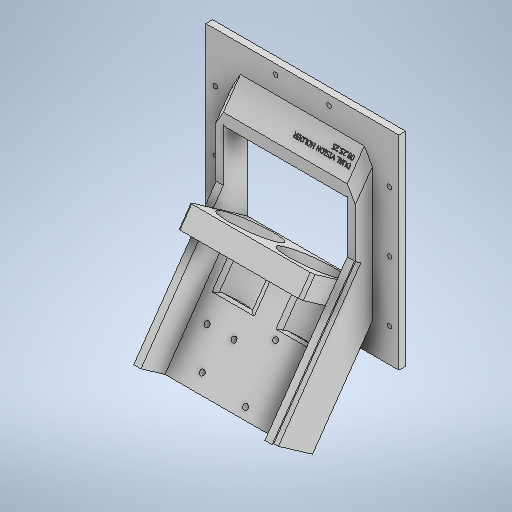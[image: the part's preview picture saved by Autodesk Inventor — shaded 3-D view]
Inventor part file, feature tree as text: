
AUTODESK INVENTOR PART (.ipt)
format: ipt  version: 2025.3 (Build 293356030, 356C)  size: 1,626,112 bytes
history: native  units: in
note: dims shown in document units (in); Inventor stores cm internally (conversion verified against a paired STEP export)
features: sketch x58, extrude x53, projected_geometry x13, plane x5, chamfer x3, move_body x1, hole x1
ambient origin geometry x8: Origin, YZ Plane, XZ Plane, XY Plane, X Axis, Y Axis, Z Axis, Center Point
bodies: Solid1 (feature_tree)
feature tree (134):
  extrude  "Extrusion1"  Depth=0.1969in TaperAngle=0.0deg
  move_body  "Move Body1"
  plane  "Work Plane1"
  sketch  "Sketch5"  dims[d5=1.7717in d6=1.7717in d7=1.7717in d8=1.7717in d9=0.8108in d10=90.0deg d11=0.0787in d12=0.3701in d13=0.4252in d14=0.1362in d15=-0.0984in d16=-0.0591in d17=0.0in]
  plane  "Work Plane2"
  extrude  "Extrusion4"  TaperAngle=0.0deg  [1 undecoded]
  extrude  "Extrusion6"  Depth=0.2405in
  extrude  "Extrusion8"  Depth=2.7559in TaperAngle=0.0deg
  chamfer  "Chamfer1"  [1 undecoded]
  extrude  "Extrusion11"  Depth=0.2362in
  plane  "Work Plane3"
  extrude  "Extrusion13"  Depth=0.1969in TaperAngle=0.0deg
  plane  "Work Plane4"
  plane  "Work Plane6"
  extrude  "Extrusion21"  Depth=0.5027in
  extrude  "Extrusion22"  Depth=0.5027in
  extrude  "Extrusion25"  Depth=1.1811in TaperAngle=0.0deg
  extrude  "Extrusion26"  Depth=0.1969in
  sketch  "Sketch33"  dims[d100=3.6403in d101=2.7717in]
  extrude  "Extrusion27"  Depth=0.2362in TaperAngle=0.0deg
  extrude  "Extrusion29"  Depth=3.6403in
  extrude  "Extrusion28"  Depth=0.6299in TaperAngle=0.0deg
  sketch  "Sketch36"  dims[d124=0.9712in d125=0.0in d126=0.5906in d127=0.0in]
  extrude  "Extrusion30"  Depth=0.7874in
  extrude  "Extrusion31"  Depth=0.5906in TaperAngle=0.0deg
  sketch  "Sketch39"  dims[d164=0.1181in d165=0.0in d168=0.5906in d169=0.0in]
  extrude  "Extrusion35"  Depth=11.3469in TaperAngle=0.0deg
  sketch  "Sketch45"  dims[d176=0.7313in d177=0.0in d186=0.0in d187=0.0in]
  extrude  "Extrusion37"  Depth=0.1181in TaperAngle=0.0deg
  extrude  "Extrusion38"  Depth=0.1181in TaperAngle=0.0deg
  extrude  "Extrusion40"  TaperAngle=0.0deg  [1 undecoded]
  extrude  "Extrusion41"  TaperAngle=0.0deg  [1 undecoded]
  extrude  "Extrusion43"  TaperAngle=0.0deg  [1 undecoded]
  extrude  "Extrusion44"  Depth=0.0394in TaperAngle=0.0deg
  extrude  "Extrusion46"  Depth=3.9671in TaperAngle=0.0deg
  extrude  "Name Extrusion"  Depth=0.1969in
  extrude  "Extrusion48"  TaperAngle=60.0deg  [1 undecoded]
  sketch  "Sketch61"  dims[d257=0.1181in d258=0.0in d259=0.0787in d260=0.0in]
  extrude  "Extrusion50"  Depth=0.1969in
  extrude  "Extrusion51"  Depth=0.3937in
  extrude  "Extrusion52"  Depth=0.3937in
  extrude  "Extrusion53"  Depth=0.0787in TaperAngle=0.0deg
  extrude  "Extrusion54"  Depth=0.3937in TaperAngle=0.0deg
  extrude  "Extrusion57"  TaperAngle=0.0deg  [1 undecoded]
  extrude  "Extrusion59"  Depth=0.9449in
  extrude  "Extrusion60"  TaperAngle=0.0deg  [1 undecoded]
  extrude  "Event Cam Hole"  Depth=1.1614in
  extrude  "Extrusion62"  Depth=0.6299in TaperAngle=0.0deg
  extrude  "Extrusion63"  Depth=0.1969in TaperAngle=0.0deg
  extrude  "Extrusion64"  Depth=0.1181in TaperAngle=0.0deg
  extrude  "Extrusion65"  Depth=0.1575in
  extrude  "Extrusion70"  Depth=0.1575in
  extrude  "Extrusion74"  Depth=0.1575in
  extrude  "Extrusion76"  Depth=0.1575in
  extrude  "Extrusion77"  Depth=3.6405in
  extrude  "Extrusion78"  Depth=0.2756in
  extrude  "Extrusion81"  Depth=0.1181in TaperAngle=0.0deg
  chamfer  "Chamfer3"  Distance=0.1956in
  extrude  "Extrusion82"  TaperAngle=0.0deg  [1 undecoded]
  extrude  "Extrusion83"  Depth=0.0787in TaperAngle=45.0deg
  extrude  "Extrusion84"  Depth=0.3543in
  extrude  "Extrusion85"  Depth=0.3543in
  extrude  "Extrusion86"  Depth=0.1181in
  chamfer  "Chamfer4"  Distance=0.0984in
  extrude  "Extrusion87"  TaperAngle=0.0deg  [1 undecoded]
  extrude  "Extrusion88"  Depth=1.0236in TaperAngle=0.0deg
  sketch  "Sketch107"  dims[d398=0.3937in]
  extrude  "Extrusion89"  Depth=0.3937in TaperAngle=0.0deg
  extrude  "Extrusion90"  Depth=0.3937in
  sketch  "Sketch1"  dims[d1=0.5512in d2=0.1969in d3=0.0in]
  sketch  "Sketch6"  dims[d18=0.2749in d24=0.2405in]
  sketch  "Sketch8"  dims[d25=2.7559in d26=0.0in d29=2.5591in d30=0.0in d36=0.0in d37=0.0in]
  sketch  "Sketch12"  dims[d42=0.2362in d43=0.2362in]
  sketch  "Sketch15"  dims[d52=0.2362in d53=0.0787in d54=45.0deg d55=0.1969in d56=0.0in]
  sketch  "Sketch17"  dims[d59=0.5906in d60=0.0in d76=0.5027in]
  sketch  "Sketch27"  dims[d77=0.5027in d78=0.5027in]
  sketch  "Sketch28"  dims[d79=0.5027in d81=1.1811in d82=0.0in]
  sketch  "Sketch31"  dims[d83=0.0in d84=0.0in d91=0.1969in]
  sketch  "Sketch32"  dims[d94=0.2362in d95=0.0in d96=0.2362in d97=0.0in]
  sketch  "Sketch34"  dims[d112=1.9685in d113=0.6299in d114=0.0in]
  sketch  "Sketch35"  dims[d115=0.1575in d117=0.1575in d122=0.7874in d123=0.9331in]
  sketch  "Sketch37"  dims[d128=11.3469in d129=0.0in d130=11.3469in d131=0.0in]
  sketch  "Sketch38"  dims[d141=0.6299in d156=0.1181in d157=0.0in]
  sketch  "Sketch44"  dims[d170=4.7244in d171=0.0in d174=0.0in d175=0.0in]
  projected_geometry  "Projected Loop2"
  projected_geometry  "Projected Loop3"
  projected_geometry  "Projected Loop5"
  sketch  "Sketch47"  dims[d188=0.0in d189=0.0in d194=0.0in d195=0.0in]
  sketch  "Sketch49"  dims[d198=0.0591in d199=0.0in d200=0.0394in d201=0.0in]
  sketch  "Sketch50"  dims[d235=6.1063in d236=0.0in d244=3.9671in d245=0.0in]
  sketch  "Sketch52"  dims[d246=0.9963in d248=0.1969in]
  sketch  "Sketch53"  dims[d249=0.1378in d250=60.0deg]
  sketch  "Sketch56"  dims[d251=0.1969in d252=0.1378in]
  sketch  "Sketch58"  dims[d253=60.0deg d254=0.3937in]
  sketch  "Sketch59"  dims[d255=0.3937in d256=0.3937in]
  sketch  "Sketch63"  dims[d261=1.9685in d262=0.0in d271=0.3937in d272=0.0in]
  sketch  "Sketch64"  dims[d275=0.3937in d276=0.0in d277=0.0in d278=0.0in]
  sketch  "Sketch65"  dims[d279=1.6142in d280=0.9449in]
  sketch  "Sketch66"  dims[d281=1.2598in d282=0.0in d283=0.0in]
  sketch  "Sketch67"  dims[d284=1.5748in d287=1.1614in]
  sketch  "Sketch70"  dims[d288=0.8512in d289=0.6299in d290=0.0in]
  sketch  "Sketch72"  dims[d291=2.9921in d292=0.0in d293=0.1969in d294=0.0in]
  sketch  "Sketch75"  dims[d295=0.1181in d296=0.0in d314=0.0197in d315=0.0in]
  sketch  "Sketch76"  dims[d331=0.3937in d332=0.1575in]
  sketch  "Sketch77"  dims[d333=0.1575in d334=1.0236in]
  sketch  "Sketch79"  dims[d335=0.1575in d336=1.5354in]
  projected_geometry  "Projected Loop11"
  sketch  "Sketch80"  dims[d337=0.1575in d338=1.0236in]
  projected_geometry  "Projected Loop12"
  sketch  "Sketch81"  dims[d339=3.6405in d340=0.0in d347=0.2756in]
  sketch  "Sketch86"  dims[d348=0.2756in d349=0.2756in]
  projected_geometry  "Projected Loop14"
  sketch  "Sketch90"  dims[d351=0.2756in d352=0.1181in d353=0.0in d354=0.1956in d355=0.0in]
  sketch  "Sketch94"  dims[d356=0.0197in d357=0.0in d358=0.0in]
  sketch  "Sketch95"  dims[d363=3.6403in d364=0.0in d365=0.0787in d366=0.0787in d367=45.0deg]
  projected_geometry  "Projected Loop15"
  projected_geometry  "Projected Loop16"
  sketch  "Sketch96"  dims[d371=0.3543in d372=0.3543in]
  sketch  "Sketch99"  dims[d373=0.3543in d374=0.3543in]
  sketch  "Sketch100"  dims[d375=0.1181in d376=0.1181in d377=0.0984in d378=0.0in]
  sketch  "Sketch101"  dims[d379=0.067in d380=0.0in d381=0.0in d382=0.0in]
  projected_geometry  "Projected Loop17"
  sketch  "Sketch102"  dims[d383=1.0236in d384=0.0in d385=1.0236in d386=0.0in]
  projected_geometry  "Projected Loop18"
  sketch  "Sketch103"  dims[d387=0.0787in d388=0.0787in d389=45.0deg d390=0.3937in d391=0.0in]
  projected_geometry  "Projected Loop19"
  sketch  "Sketch104"  dims[d392=0.3937in d393=0.0in d394=0.3937in]
  projected_geometry  "Projected Loop20"
  sketch  "Sketch105"  dims[d395=0.3937in d396=0.3937in]
  sketch  "Sketch106"  dims[d397=0.3937in]
  sketch  "Sketch108"  dims[d399=0.3937in d400=0.3937in d401=0.0787in d402=0.0in d403=0.1181in d404=0.0in d38=0.0197in d39=0.0344in d57=0.0197in d58=0.0344in d158=0.0197in d159=0.0344in d178=0.0in d179=0.0in d180=0.0in d181=0.0in d202=0.0197in d203=0.0344in d359=0.0344in]
  projected_geometry  "Projected Loop21"
  sketch  "Sketch2"  dims[d4=0.315in]
  hole  "Hole1"  [1 undecoded]
note: 11 required parameter values undecoded (feature->parameter linkage not recoverable at this tier; creation-order binding heuristic only, values carry confidence <= 0.55)
